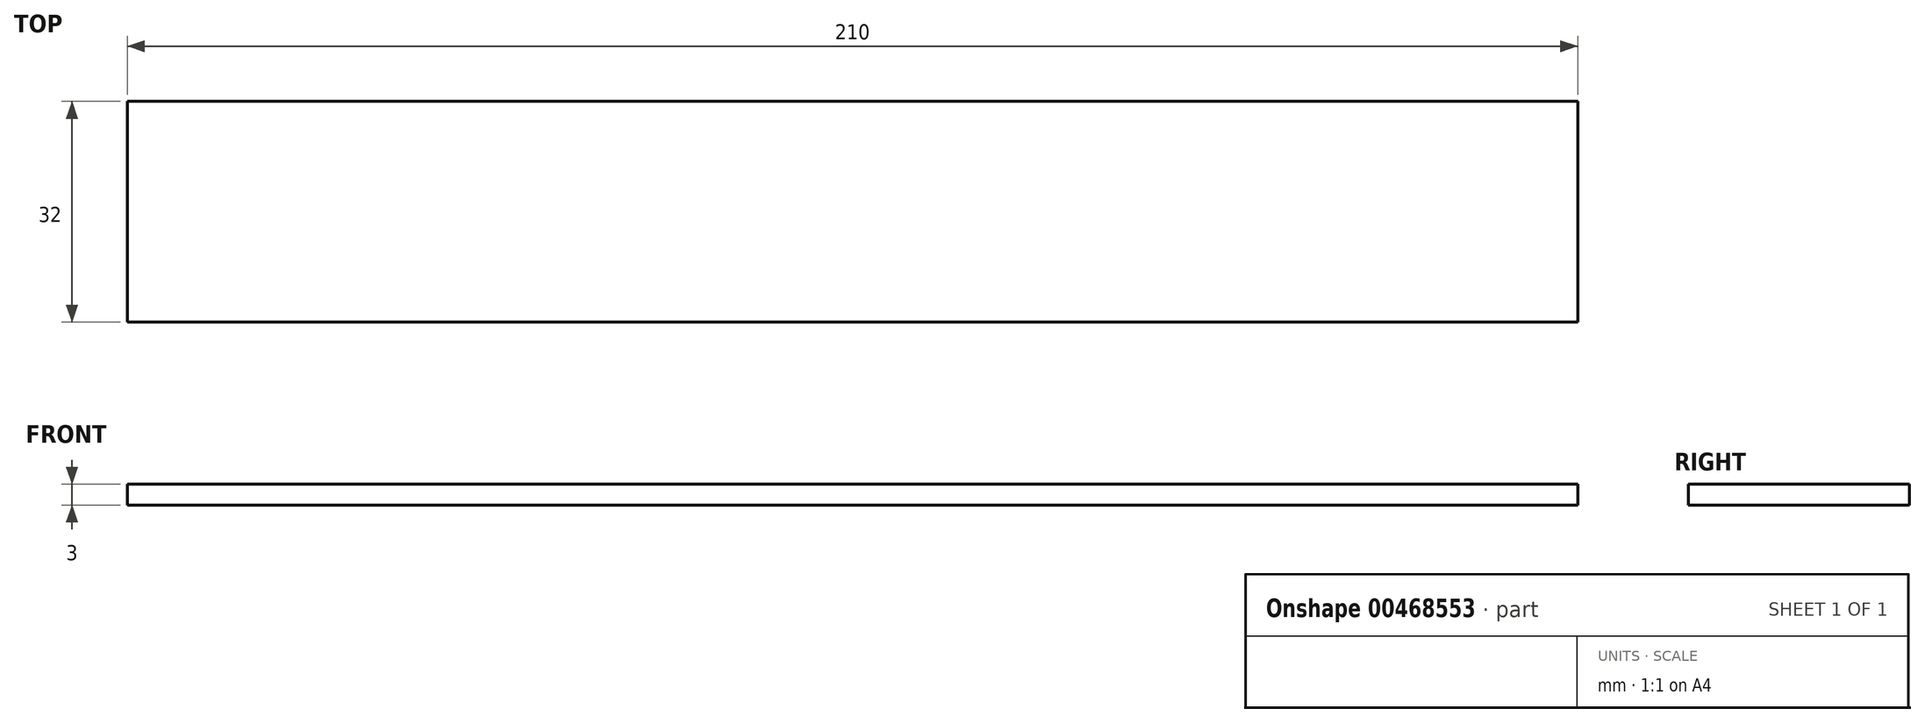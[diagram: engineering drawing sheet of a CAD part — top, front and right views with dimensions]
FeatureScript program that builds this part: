
annotation { "Feature Type Name" : "Feature", "Feature Type Description" : "" }
export const myFeature = defineFeature(function(context is Context, id is Id, definition is map)
    precondition{}
    {
        {
            var Q0;
            Q0=qCreatedBy(makeId("Top.planeOp"),FACE);
            var sketch = newSketch(context, id + "F0", { "sketchPlane" : qUnion([Q0])});
            skLineSegment(sketch, "E0.bottom", {"start": v(-96, 17.36) * mm, "end": v(114, 17.36) * mm});
            skLineSegment(sketch, "E0.top", {"start": v(-96, -14.64) * mm, "end": v(114, -14.64) * mm});
            skLineSegment(sketch, "E0.left", {"start": v(-96, 17.36) * mm, "end": v(-96, -14.64) * mm});
            skLineSegment(sketch, "E0.right", {"start": v(114, 17.36) * mm, "end": v(114, -14.64) * mm});
            skSolve(sketch);
        }
        {
            var Q0;
            Q0=makeQuery(id+"F0.imprint","IMPRINT",FACE,{"disambiguationData":[TD([[makeQuery(id+"F0.imprint","IMPRINT",EDGE,{"derivedFrom":sQuery(id+"F0.wireOp",EDGE,"E0.bottom")}),-1.0]])]});
            extrude(context, id + "F1", {"entities" : qUnion([Q0]), "depth" : 3 * mm, "offsetDistance" : 25 * mm});
        }
    });
